annotation { "Feature Type Name" : "Feature", "Feature Type Description" : "" }
export const myFeature = defineFeature(function(context is Context, id is Id, definition is map)
    precondition{}
    {
        {
            var Q0;
            Q0=qCreatedBy(makeId("Front.planeOp"),FACE);
            var sketch = newSketch(context, id + "F0", { "sketchPlane" : qUnion([Q0])});
            skLineSegment(sketch, "E0.bottom", {"start": v(-50.66, 38.1) * mm, "end": v(25.54, 38.1) * mm});
            skLineSegment(sketch, "E0.top", {"start": v(-50.66, 0) * mm, "end": v(25.54, 0) * mm});
            skLineSegment(sketch, "E0.left", {"start": v(-50.66, 38.1) * mm, "end": v(-50.66, 0) * mm});
            skLineSegment(sketch, "E0.right", {"start": v(25.54, 38.1) * mm, "end": v(25.54, 0) * mm});
            skLineSegment(sketch, "E1.bottom", {"start": v(46.68, -3.31) * mm, "end": v(56, -3.31) * mm});
            skLineSegment(sketch, "E1.top", {"start": v(46.68, -6.7) * mm, "end": v(56, -6.7) * mm});
            skLineSegment(sketch, "E1.left", {"start": v(46.68, -3.31) * mm, "end": v(46.68, -6.7) * mm});
            skLineSegment(sketch, "E1.right", {"start": v(56, -3.31) * mm, "end": v(56, -6.7) * mm});
            skLineSegment(sketch, "E2", {"start": v(50.66, -28.89) * mm, "end": v(50.66, -45.85) * mm});
            skLineSegment(sketch, "E3.bottom", {"start": v(47.94, -52.75) * mm, "end": v(54, -52.75) * mm});
            skLineSegment(sketch, "E3.top", {"start": v(47.94, -45.85) * mm, "end": v(54, -45.85) * mm});
            skLineSegment(sketch, "E3.left", {"start": v(47.94, -52.75) * mm, "end": v(47.94, -45.85) * mm});
            skLineSegment(sketch, "E3.right", {"start": v(54, -52.75) * mm, "end": v(54, -45.85) * mm});
            skText(sketch, "E4", { "text": "Solar Panel", "fontName": "OpenSans-Regular.ttf"});
            skText(sketch, "E5", { "text": "Power Cord\n", "fontName": "OpenSans-Regular.ttf"});
            skText(sketch, "E6", { "text": "Standard Wire\n", "fontName": "OpenSans-Regular.ttf"});
            skText(sketch, "E7", { "text": "USB 3 Power Cord", "fontName": "OpenSans-Regular.ttf"});
            skText(sketch, "E8", { "text": "7805 regulator chip\n", "fontName": "OpenSans-Regular.ttf"});
            skLineSegment(sketch, "E9.left", {"start": v(56, -6.7) * mm, "end": v(56, -4.98) * mm});
            skLineSegment(sketch, "E10", {"start": v(56, -6.7) * mm, "end": v(50.66, -28.89) * mm});
            skLineSegment(sketch, "E11", {"start": v(56, -3.31) * mm, "end": v(50.66, -28.89) * mm});
            skLineSegment(sketch, "E12", {"start": v(46.44, -4.85) * mm, "end": v(25.7, 3.9) * mm});
            skText(sketch, "E13", { "text": "1:3 scale\n", "fontName": "OpenSans-Regular.ttf"});
            const initialGuessF0  = {"E4": [-0.03412, 0.01758, 1, 0, 0.00607], "E5": [0.05778, -0.04375, 1, 0, 0.0069], "E6": [0.03977, 0.04015, 1, 0, 0.00733], "E7": [-0.10666, -0.05613, 1, 0, 0.01256], "E8": [0.07906, 0.01585, 1, 0, 0.0107], "E13": [0.0979, 0.08387, 1, 0, 0.01245]};
            skSetInitialGuess(sketch, initialGuessF0);
            skSolve(sketch);
        }
        {
            var Q0;
            Q0 = qSketchRegion(id + "F0", true);
            extrude(context, id + "F1", {"entities" : qUnion([Q0]), "depth" : 25.4 * mm, "offsetDistance" : 25.4 * mm});
        }
    });